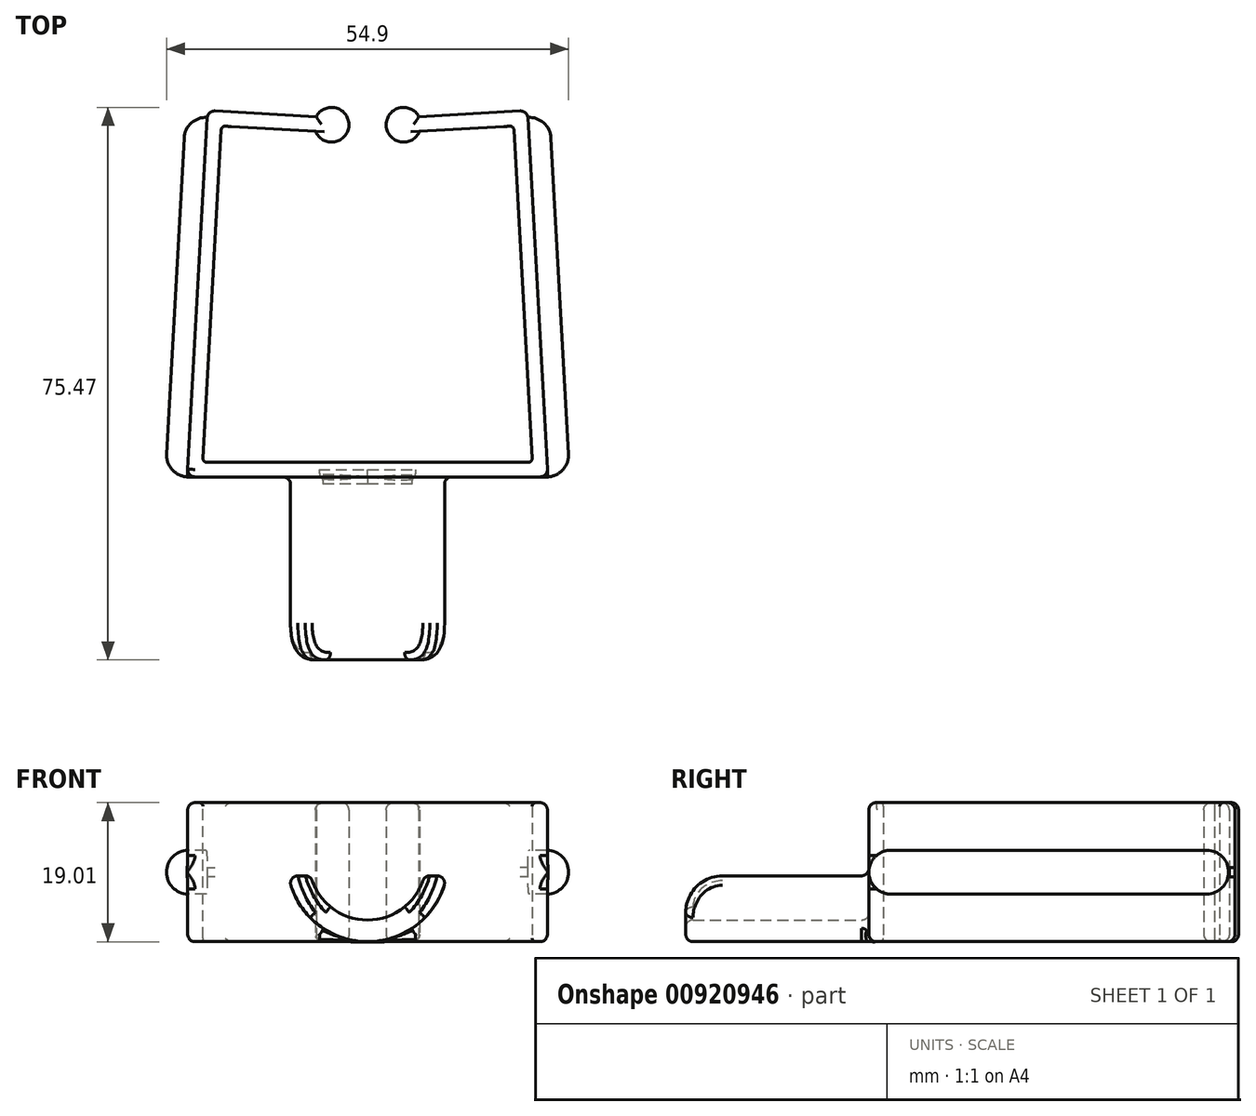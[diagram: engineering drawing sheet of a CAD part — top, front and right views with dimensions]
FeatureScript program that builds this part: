
annotation { "Feature Type Name" : "Feature", "Feature Type Description" : "" }
export const myFeature = defineFeature(function(context is Context, id is Id, definition is map)
    precondition{}
    {
        {
            var Q0;
            Q0=qCreatedBy(makeId("Top.planeOp"),FACE);
            var sketch = newSketch(context, id + "F0", { "sketchPlane" : qUnion([Q0])});
            skLineSegment(sketch, "E0", {"start": v(0, -31.5) * mm, "end": v(22.5, -31.5) * mm});
            skLineSegment(sketch, "E1", {"start": v(19.95, 14.44) * mm, "end": v(22.5, -31.5) * mm});
            skLineSegment(sketch, "E2", {"start": v(19.95, 14.44) * mm, "end": v(7.12, 13.72) * mm});
            skLineSegment(sketch, "E3.0", {"start": v(0, -33.5) * mm, "end": v(24.62, -33.5) * mm});
            skLineSegment(sketch, "E4.0", {"start": v(21.84, 16.54) * mm, "end": v(24.62, -33.5) * mm});
            skLineSegment(sketch, "E5.0", {"start": v(21.84, 16.54) * mm, "end": v(7.01, 15.72) * mm});
            skLineSegment(sketch, "E6.MirrorCS", {"start": v(-21.83, 16.54) * mm, "end": v(-7, 15.72) * mm});
            skLineSegment(sketch, "E7.MirrorCS", {"start": v(-19.95, 14.44) * mm, "end": v(-7.12, 13.72) * mm});
            skLineSegment(sketch, "E8.MirrorCS", {"start": v(-21.88, 15.61) * mm, "end": v(-24.61, -33.5) * mm});
            skLineSegment(sketch, "E9.MirrorCS", {"start": v(-20, 13.5) * mm, "end": v(-22.5, -31.5) * mm});
            skLineSegment(sketch, "E10.MirrorCS", {"start": v(0, -31.5) * mm, "end": v(-22.5, -31.5) * mm});
            skLineSegment(sketch, "E11.MirrorCS", {"start": v(0, -33.5) * mm, "end": v(-24.61, -33.5) * mm});
            skArc(sketch, "E12", {"start": v(7.01, 15.72) * mm, "mid": v(2.55, 14.47) * mm, "end": v(7.12, 13.72) * mm});
            skArc(sketch, "E13.MirrorC", {"start": v(-7, 15.72) * mm, "mid": v(-2.54, 14.47) * mm, "end": v(-7.12, 13.72) * mm});
            skLineSegment(sketch, "E14", {"start": v(-21.88, 15.61) * mm, "end": v(-21.83, 16.54) * mm});
            skLineSegment(sketch, "E15", {"start": v(-20, 13.5) * mm, "end": v(-19.95, 14.44) * mm});
            skSolve(sketch);
        }
        {
            var Q0;
            Q0=makeQuery(id+"F0.imprint","IMPRINT",FACE,{"disambiguationData":[TD([[makeQuery(id+"F0.imprint","IMPRINT",EDGE,{"derivedFrom":sQuery(id+"F0.wireOp",EDGE,"E0")}),-1.0]])]});
            extrude(context, id + "F1", {"entities" : qUnion([Q0]), "depth" : 19 * mm, "offsetDistance" : 25 * mm});
        }
        {
            var Q0;
            Q0=makeQuery(id+"F1.opExtrude","SWEPT_FACE",FACE,{"disambiguationData":[OSD([sQuery(id+"F0.wireOp",EDGE,"E8.MirrorCS")])]});
            var sketch = newSketch(context, id + "F2", { "sketchPlane" : qUnion([Q0])});
            skLineSegment(sketch, "E16", {"start": v(-14.38, 12.5) * mm, "end": v(34.8, 12.5) * mm});
            skLineSegment(sketch, "E17", {"start": v(-14.38, 6.5) * mm, "end": v(34.8, 6.5) * mm});
            skLineSegment(sketch, "E18", {"start": v(-14.38, 12.5) * mm, "end": v(-14.38, 6.5) * mm});
            skLineSegment(sketch, "E19", {"start": v(34.8, 12.5) * mm, "end": v(34.8, 6.5) * mm});
            skSolve(sketch);
        }
        {
            var Q0;
            Q0=makeQuery(id+"F2.imprint","IMPRINT",FACE,{"disambiguationData":[TD([[makeQuery(id+"F2.imprint","IMPRINT",EDGE,{"derivedFrom":sQuery(id+"F2.wireOp",EDGE,"E16")}),-1.0]])]});
            extrude(context, id + "F3", {"entities" : qUnion([Q0]), "operationType" : NewBodyOperationType.ADD, "depth" : 3 * mm, "offsetDistance" : 25 * mm});
        }
        {
            var Q0;
            Q0=makeQuery(id+"F1.opExtrude","SWEPT_FACE",FACE,{"disambiguationData":[OSD([sQuery(id+"F0.wireOp",EDGE,"E4.0")])]});
            var sketch = newSketch(context, id + "F4", { "sketchPlane" : qUnion([Q0])});
            skLineSegment(sketch, "E20", {"start": v(-34.8, 12.5) * mm, "end": v(14.38, 12.5) * mm});
            skLineSegment(sketch, "E21", {"start": v(-34.8, 6.5) * mm, "end": v(14.38, 6.5) * mm});
            skLineSegment(sketch, "E22", {"start": v(-34.8, 12.5) * mm, "end": v(-34.8, 6.5) * mm});
            skLineSegment(sketch, "E23", {"start": v(14.38, 12.5) * mm, "end": v(14.38, 6.5) * mm});
            skSolve(sketch);
        }
        {
            var Q0;
            Q0=makeQuery(id+"F4.imprint","IMPRINT",FACE,{"disambiguationData":[TD([[makeQuery(id+"F4.imprint","IMPRINT",EDGE,{"derivedFrom":sQuery(id+"F4.wireOp",EDGE,"E20")}),-1.0]])]});
            extrude(context, id + "F5", {"entities" : qUnion([Q0]), "operationType" : NewBodyOperationType.ADD, "depth" : 3 * mm, "offsetDistance" : 25 * mm});
        }
        {
            var Q0;
            Q0=makeQuery(id+"F5.opExtrude","CAP_EDGE",EDGE,{"disambiguationData":[OSD([sQuery(id+"F4.wireOp",EDGE,"E20")])],"isStart":false});
            var Q1;
            Q1=makeQuery(id+"F5.opExtrude","CAP_EDGE",EDGE,{"disambiguationData":[OSD([sQuery(id+"F4.wireOp",EDGE,"E21")])],"isStart":false});
            var Q2;
            Q2=makeQuery(id+"F5.opExtrude","CAP_EDGE",EDGE,{"disambiguationData":[OSD([sQuery(id+"F4.wireOp",EDGE,"E22")])],"isStart":false});
            var Q3;
            Q3=makeQuery(id+"F5.opExtrude","SWEPT_EDGE",EDGE,{"disambiguationData":[OSD([sQuery(id+"F0.wireOp",EDGE,"E3.0"),sQuery(id+"F0.wireOp",EDGE,"E4.0"),sQuery(id+"F4.wireOp",EDGE,"E20"),sQuery(id+"F4.wireOp",EDGE,"E22")])]});
            var Q4;
            Q4=makeQuery(id+"F5.opExtrude","SWEPT_EDGE",EDGE,{"disambiguationData":[OSD([sQuery(id+"F0.wireOp",EDGE,"E3.0"),sQuery(id+"F0.wireOp",EDGE,"E4.0"),sQuery(id+"F4.wireOp",EDGE,"E21"),sQuery(id+"F4.wireOp",EDGE,"E22")])]});
            var Q5;
            Q5=makeQuery(id+"F5.opExtrude","CAP_EDGE",EDGE,{"disambiguationData":[OSD([sQuery(id+"F4.wireOp",EDGE,"E23")])],"isStart":false});
            var Q6;
            Q6=makeQuery(id+"F5.opExtrude","SWEPT_EDGE",EDGE,{"disambiguationData":[OSD([sQuery(id+"F0.wireOp",EDGE,"E4.0"),sQuery(id+"F0.wireOp",EDGE,"E5.0"),sQuery(id+"F4.wireOp",EDGE,"E20"),sQuery(id+"F4.wireOp",EDGE,"E23")])]});
            var Q7;
            Q7=makeQuery(id+"F5.opExtrude","SWEPT_EDGE",EDGE,{"disambiguationData":[OSD([sQuery(id+"F0.wireOp",EDGE,"E4.0"),sQuery(id+"F0.wireOp",EDGE,"E5.0"),sQuery(id+"F4.wireOp",EDGE,"E21"),sQuery(id+"F4.wireOp",EDGE,"E23")])]});
            var Q8;
            Q8=makeQuery(id+"F3.opExtrude","CAP_EDGE",EDGE,{"disambiguationData":[OSD([sQuery(id+"F2.wireOp",EDGE,"E16")])],"isStart":false});
            var Q9;
            Q9=makeQuery(id+"F3.opExtrude","CAP_EDGE",EDGE,{"disambiguationData":[OSD([sQuery(id+"F2.wireOp",EDGE,"E17")])],"isStart":false});
            var Q10;
            Q10=makeQuery(id+"F3.opExtrude","CAP_EDGE",EDGE,{"disambiguationData":[OSD([sQuery(id+"F2.wireOp",EDGE,"E18")])],"isStart":false});
            var Q11;
            Q11=makeQuery(id+"F3.opExtrude","SWEPT_EDGE",EDGE,{"disambiguationData":[OSD([sQuery(id+"F0.wireOp",EDGE,"E6.MirrorCS"),sQuery(id+"F0.wireOp",EDGE,"E8.MirrorCS"),sQuery(id+"F2.wireOp",EDGE,"E17"),sQuery(id+"F2.wireOp",EDGE,"E18")])]});
            var Q12;
            Q12=makeQuery(id+"F3.opExtrude","SWEPT_EDGE",EDGE,{"disambiguationData":[OSD([sQuery(id+"F0.wireOp",EDGE,"E6.MirrorCS"),sQuery(id+"F0.wireOp",EDGE,"E8.MirrorCS"),sQuery(id+"F2.wireOp",EDGE,"E16"),sQuery(id+"F2.wireOp",EDGE,"E18")])]});
            var Q13;
            Q13=makeQuery(id+"F3.opExtrude","CAP_EDGE",EDGE,{"disambiguationData":[OSD([sQuery(id+"F2.wireOp",EDGE,"E19")])],"isStart":false});
            var Q14;
            Q14=makeQuery(id+"F3.opExtrude","SWEPT_EDGE",EDGE,{"disambiguationData":[OSD([sQuery(id+"F0.wireOp",EDGE,"E8.MirrorCS"),sQuery(id+"F0.wireOp",EDGE,"E11.MirrorCS"),sQuery(id+"F2.wireOp",EDGE,"E16"),sQuery(id+"F2.wireOp",EDGE,"E19")])]});
            var Q15;
            Q15=makeQuery(id+"F3.opExtrude","SWEPT_EDGE",EDGE,{"disambiguationData":[OSD([sQuery(id+"F0.wireOp",EDGE,"E8.MirrorCS"),sQuery(id+"F0.wireOp",EDGE,"E11.MirrorCS"),sQuery(id+"F2.wireOp",EDGE,"E17"),sQuery(id+"F2.wireOp",EDGE,"E19")])]});
            fillet(context, id + "F6", {"entities" : qUnion([Q0, Q1, Q2, Q3, Q4, Q5, Q6, Q7, Q8, Q9, Q10, Q11, Q12, Q13, Q14, Q15]), "radius" : 3 * mm, "tangentPropagation" : true, "allowEdgeOverflow" : false});
        }
        {
            var Q0;
            Q0=makeQuery(id+"F1.opExtrude","SWEPT_FACE",FACE,{"disambiguationData":[OSD([sQuery(id+"F0.wireOp",EDGE,"E3.0"),sQuery(id+"F0.wireOp",EDGE,"E11.MirrorCS")])]});
            var sketch = newSketch(context, id + "F7", { "sketchPlane" : qUnion([Q0])});
            skArc(sketch, "E24", {"start": v(-7.75, 9) * mm, "mid": v(0, 2.97) * mm, "end": v(7.75, 9) * mm});
            skLineSegment(sketch, "E25", {"start": v(-7.75, 9) * mm, "end": v(-10.79, 9) * mm});
            skArc(sketch, "E26", {"start": v(0, 0) * mm, "mid": v(-7.02, 2.55) * mm, "end": v(-10.79, 9) * mm});
            skArc(sketch, "E27.MirrorCS", {"start": v(0, 0) * mm, "mid": v(7.02, 2.55) * mm, "end": v(10.79, 9) * mm});
            skLineSegment(sketch, "E28.MirrorCS", {"start": v(7.75, 9) * mm, "end": v(10.79, 9) * mm});
            skSolve(sketch);
        }
        {
            var Q0;
            Q0=makeQuery(id+"F7.imprint","IMPRINT",FACE,{"disambiguationData":[TD([[makeQuery(id+"F7.imprint","IMPRINT",EDGE,{"derivedFrom":sQuery(id+"F7.wireOp",EDGE,"E24")}),-1.0]])]});
            extrude(context, id + "F8", {"entities" : qUnion([Q0]), "operationType" : NewBodyOperationType.ADD, "depth" : 25 * mm, "offsetDistance" : 25 * mm});
        }
        {
            var Q0;
            Q0=makeQuery(id+"F8.opExtrude","CAP_EDGE",EDGE,{"disambiguationData":[OSD([sQuery(id+"F7.wireOp",EDGE,"E24")])],"isStart":false});
            var Q1;
            Q1=makeQuery(id+"F8.opExtrude","CAP_EDGE",EDGE,{"disambiguationData":[OSD([sQuery(id+"F7.wireOp",EDGE,"E26"),sQuery(id+"F7.wireOp",EDGE,"E27.MirrorCS")])],"isStart":false});
            var Q2;
            Q2=makeQuery(id+"F8.opExtrude","SWEPT_EDGE",EDGE,{"disambiguationData":[OSD([sQuery(id+"F7.wireOp",EDGE,"E24"),sQuery(id+"F7.wireOp",EDGE,"E28.MirrorCS")])]});
            var Q3;
            Q3=makeQuery(id+"F8.opExtrude","SWEPT_EDGE",EDGE,{"disambiguationData":[OSD([sQuery(id+"F7.wireOp",EDGE,"E27.MirrorCS"),sQuery(id+"F7.wireOp",EDGE,"E28.MirrorCS")])]});
            var Q4;
            Q4=makeQuery(id+"F8.opExtrude","SWEPT_EDGE",EDGE,{"disambiguationData":[OSD([sQuery(id+"F7.wireOp",EDGE,"E24"),sQuery(id+"F7.wireOp",EDGE,"E25")])]});
            var Q5;
            Q5=makeQuery(id+"F8.opExtrude","SWEPT_EDGE",EDGE,{"disambiguationData":[OSD([sQuery(id+"F7.wireOp",EDGE,"E25"),sQuery(id+"F7.wireOp",EDGE,"E26")])]});
            fillet(context, id + "F9", {"entities" : qUnion([Q0, Q1, Q2, Q3, Q4, Q5]), "radius" : 1 * mm, "tangentPropagation" : true, "allowEdgeOverflow" : false});
        }
        {
            var Q0;
            Q0=makeQuery(id+"F8.opExtrude","CAP_EDGE",EDGE,{"disambiguationData":[OSD([sQuery(id+"F7.wireOp",EDGE,"E25")])],"isStart":false});
            var Q1;
            Q1=makeQuery(id+"F8.opExtrude","CAP_EDGE",EDGE,{"disambiguationData":[OSD([sQuery(id+"F7.wireOp",EDGE,"E28.MirrorCS")])],"isStart":false});
            fillet(context, id + "F10", {"entities" : qUnion([Q0, Q1]), "radius" : 5 * mm, "tangentPropagation" : true, "allowEdgeOverflow" : false});
        }
        {
            var Q0;
            Q0=makeQuery(id+"F1.opExtrude","SWEPT_FACE",FACE,{"disambiguationData":[OSD([sQuery(id+"F0.wireOp",EDGE,"E1")])]});
            var Q1;
            Q1=makeQuery(id+"F1.opExtrude","SWEPT_FACE",FACE,{"disambiguationData":[OSD([sQuery(id+"F0.wireOp",EDGE,"E0"),sQuery(id+"F0.wireOp",EDGE,"E10.MirrorCS")])]});
            var Q2;
            Q2=makeQuery(id+"F1.opExtrude","SWEPT_FACE",FACE,{"disambiguationData":[OSD([sQuery(id+"F0.wireOp",EDGE,"E9.MirrorCS")])]});
            fillet(context, id + "F11", {"entities" : qUnion([Q0, Q1, Q2]), "radius" : .5 * mm, "tangentPropagation" : true, "allowEdgeOverflow" : false});
        }
        {
            var Q0;
            Q0=makeQuery(id+"F1.opExtrude","CAP_EDGE",EDGE,{"disambiguationData":[OSD([sQuery(id+"F0.wireOp",EDGE,"E6.MirrorCS")])],"isStart":false});
            var Q1;
            Q1=makeQuery(id+"F1.opExtrude","CAP_EDGE",EDGE,{"disambiguationData":[OSD([sQuery(id+"F0.wireOp",EDGE,"E13.MirrorC")])],"isStart":false});
            var Q2;
            Q2=makeQuery(id+"F1.opExtrude","CAP_EDGE",EDGE,{"disambiguationData":[OSD([sQuery(id+"F0.wireOp",EDGE,"E8.MirrorCS"),sQuery(id+"F0.wireOp",EDGE,"E14")])],"isStart":false});
            var Q3;
            Q3=makeQuery(id+"F1.opExtrude","CAP_EDGE",EDGE,{"disambiguationData":[OSD([sQuery(id+"F0.wireOp",EDGE,"E3.0"),sQuery(id+"F0.wireOp",EDGE,"E11.MirrorCS")])],"isStart":false});
            var Q4;
            Q4=makeQuery(id+"F1.opExtrude","CAP_EDGE",EDGE,{"disambiguationData":[OSD([sQuery(id+"F0.wireOp",EDGE,"E4.0")])],"isStart":false});
            var Q5;
            Q5=makeQuery(id+"F1.opExtrude","CAP_EDGE",EDGE,{"disambiguationData":[OSD([sQuery(id+"F0.wireOp",EDGE,"E5.0")])],"isStart":false});
            var Q6;
            Q6=makeQuery(id+"F1.opExtrude","CAP_EDGE",EDGE,{"disambiguationData":[OSD([sQuery(id+"F0.wireOp",EDGE,"E12")])],"isStart":false});
            var Q7;
            Q7=makeQuery(id+"F1.opExtrude","SWEPT_FACE",FACE,{"disambiguationData":[OSD([sQuery(id+"F0.wireOp",EDGE,"E3.0"),sQuery(id+"F0.wireOp",EDGE,"E11.MirrorCS")])]});
            var Q8;
            Q8=makeQuery(id+"F1.opExtrude","CAP_EDGE",EDGE,{"disambiguationData":[OSD([sQuery(id+"F0.wireOp",EDGE,"E4.0")])],"isStart":true});
            var Q9;
            Q9=makeQuery(id+"F1.opExtrude","CAP_EDGE",EDGE,{"disambiguationData":[OSD([sQuery(id+"F0.wireOp",EDGE,"E5.0")])],"isStart":true});
            var Q10;
            Q10=makeQuery(id+"F1.opExtrude","SWEPT_EDGE",EDGE,{"disambiguationData":[OSD([sQuery(id+"F0.wireOp",EDGE,"E4.0"),sQuery(id+"F0.wireOp",EDGE,"E5.0")])]});
            var Q11;
            Q11=makeQuery(id+"F1.opExtrude","CAP_EDGE",EDGE,{"disambiguationData":[OSD([sQuery(id+"F0.wireOp",EDGE,"E12")])],"isStart":true});
            var Q12;
            Q12=makeQuery(id+"F1.opExtrude","CAP_EDGE",EDGE,{"disambiguationData":[OSD([sQuery(id+"F0.wireOp",EDGE,"E13.MirrorC")])],"isStart":true});
            var Q13;
            Q13=makeQuery(id+"F1.opExtrude","CAP_EDGE",EDGE,{"disambiguationData":[OSD([sQuery(id+"F0.wireOp",EDGE,"E6.MirrorCS")])],"isStart":true});
            var Q14;
            Q14=makeQuery(id+"F1.opExtrude","CAP_EDGE",EDGE,{"disambiguationData":[OSD([sQuery(id+"F0.wireOp",EDGE,"E8.MirrorCS"),sQuery(id+"F0.wireOp",EDGE,"E14")])],"isStart":true});
            var Q15;
            Q15=makeQuery(id+"F1.opExtrude","SWEPT_EDGE",EDGE,{"disambiguationData":[OSD([sQuery(id+"F0.wireOp",EDGE,"E6.MirrorCS"),sQuery(id+"F0.wireOp",EDGE,"E14")])]});
            fillet(context, id + "F12", {"entities" : qUnion([Q0, Q1, Q2, Q3, Q4, Q5, Q6, Q7, Q8, Q9, Q10, Q11, Q12, Q13, Q14, Q15]), "radius" : 1 * mm, "tangentPropagation" : true, "allowEdgeOverflow" : false});
        }
    });
